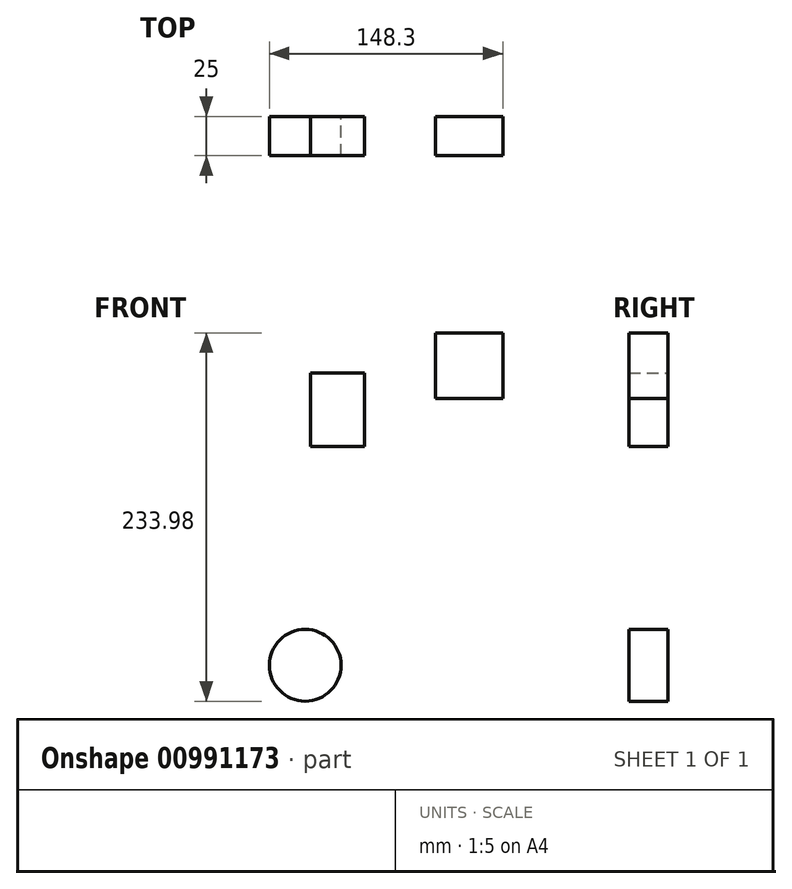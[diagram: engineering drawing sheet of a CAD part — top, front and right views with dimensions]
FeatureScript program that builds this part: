
annotation { "Feature Type Name" : "Feature", "Feature Type Description" : "" }
export const myFeature = defineFeature(function(context is Context, id is Id, definition is map)
    precondition{}
    {
        {
            var Q0;
            Q0=qCreatedBy(makeId("Front.planeOp"),FACE);
            var sketch = newSketch(context, id + "F0", { "sketchPlane" : qUnion([Q0])});
            skLineSegment(sketch, "E0.bottom", {"start": v(-122, 60.2) * mm, "end": v(-87.82, 60.2) * mm});
            skLineSegment(sketch, "E0.top", {"start": v(-122, 13.37) * mm, "end": v(-87.82, 13.37) * mm});
            skLineSegment(sketch, "E0.left", {"start": v(-122, 60.2) * mm, "end": v(-122, 13.37) * mm});
            skLineSegment(sketch, "E0.right", {"start": v(-87.82, 60.2) * mm, "end": v(-87.82, 13.37) * mm});
            skLineSegment(sketch, "E1.bottom", {"start": v(-42.81, 85.69) * mm, "end": v(0, 85.69) * mm});
            skLineSegment(sketch, "E1.top", {"start": v(-42.81, 43.9) * mm, "end": v(0, 43.9) * mm});
            skLineSegment(sketch, "E1.left", {"start": v(-42.81, 85.69) * mm, "end": v(-42.81, 43.9) * mm});
            skLineSegment(sketch, "E1.right", {"start": v(0, 85.69) * mm, "end": v(0, 43.9) * mm});
            skSolve(sketch);
        }
        {
            var Q0;
            Q0 = qSketchRegion(id + "F0", true);
            extrude(context, id + "F1", {"entities" : qUnion([Q0]), "depth" : 25 * mm, "offsetDistance" : 25 * mm});
        }
        {
            var Q0;
            Q0=qCreatedBy(makeId("Front.planeOp"),FACE);
            var sketch = newSketch(context, id + "F2", { "sketchPlane" : qUnion([Q0])});
            skCircle(sketch, "E2", {"center": v(-125.52, -125.51) * mm, "radius": 22.78 * mm});
            skSolve(sketch);
        }
        {
            var Q0;
            Q0 = qSketchRegion(id + "F2", true);
            extrude(context, id + "F3", {"entities" : qUnion([Q0]), "depth" : 25 * mm, "offsetDistance" : 25 * mm});
        }
    });
